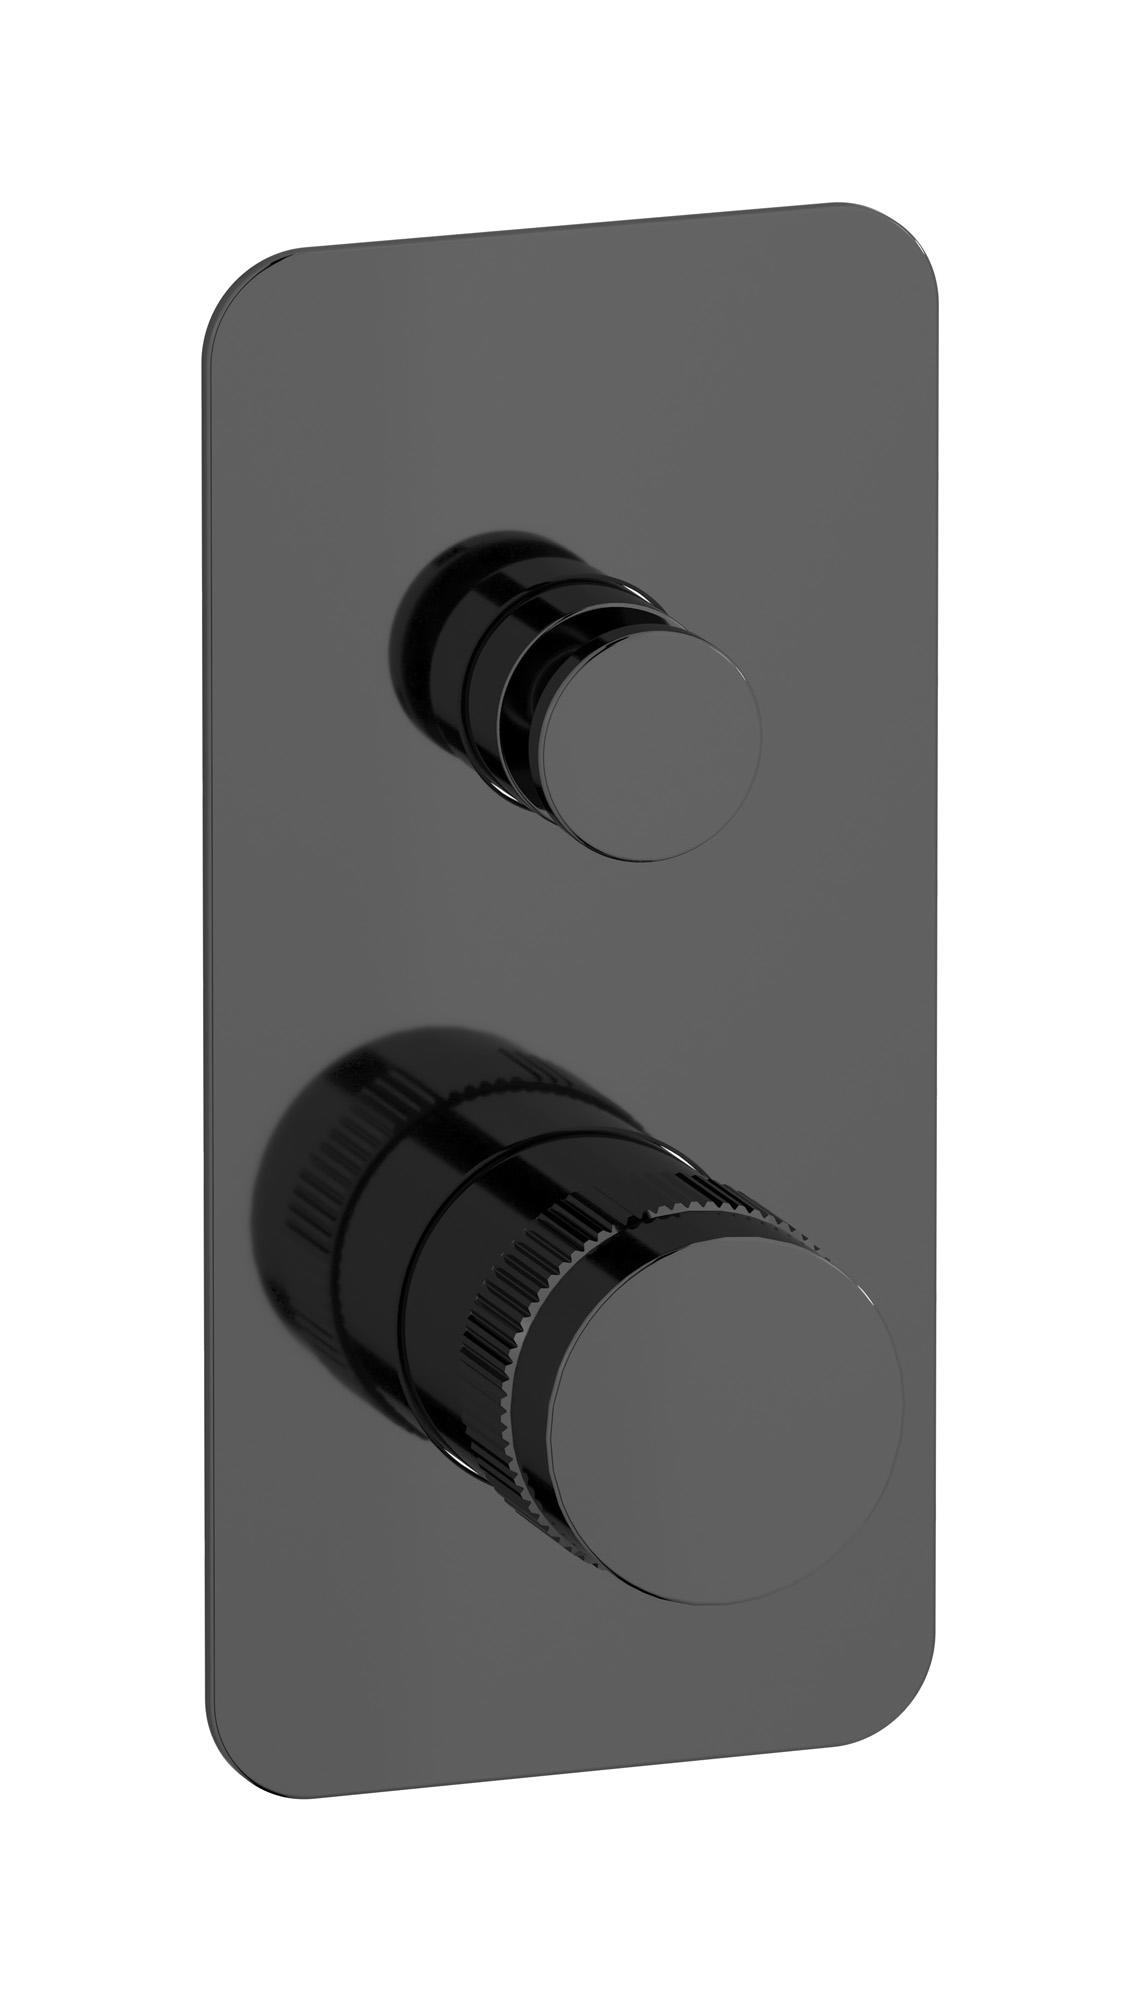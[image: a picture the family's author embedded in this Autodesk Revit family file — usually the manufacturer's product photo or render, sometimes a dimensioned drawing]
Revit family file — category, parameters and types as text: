
# Revit family: RX310
name_source: partatom
category: Apparecchi idraulici
units: mm (PartAtom-declared; Revit-internal decimal feet)

## family parameters
Basato su piano di lavoro = No
Condiviso = No
Mantieni orientamento annotazione = No
Numero OmniClass = 23.45.55.17
Punto di calcolo locali = No
Quota connettore circolare = Usa diametro
Sempre verticale = Sì
Taglio con vuoti quando caricato = No
Tipo di parte = Normale
Titolo OmniClass = Mixing Faucets

## types (12) — shared parameters
Cold water inlet = 10 mm  [stored 0.0328084 ft]
Commenti sul tipo = Exposed parts for manual wall hydroprogressive mixer with 2 ways diverter
Connessione CW = No
Connessione HW = No
Connessione di scarico = No
Connessione di ventilazione = No
Descrizione = Exposed parts for manual wall hydroprogressive mixer with 2 ways diverter
Hot water inlet = 10 mm  [stored 0.0328084 ft]
Produttore = IB Rubinetterie S.p.A.
URL = https://www.weareib.it
zero-valued in all types: Prospetto di default

## per-type parameters (varying)
| type | Finishes surface | Immagine tipo | Modello |
| Chrome | IB_Chrome | RX310CC.jpg | RX310CC |
| Black Chrome | IB_Black chrome | RX310CF.jpg | RX310CF |
| Brushed Black Chrome | IB_Brushed black chrome | RX310CS.jpg | RX310CS |
| Pale Gold | IB_Pale gold | RX310II.jpg | RX310II |
| Brushed Pale Gold | IB_brushed pale gold | RX310IS.jpg | RX310IS |
| Matt Black | IB_matt black | RX310NP.jpg | RX310NP |
| Natural Brass | IB_Brass | RX310ON.jpg | RX310ON |
| Gold | IB_gold | RX310OO.jpg | RX310OO |
| Brushed Gold | IB_brushed gold | RX310OS.jpg | RX310OS |
| Rose Gold | IB_Rose gold | RX310RS.jpg | RX310RS |
| Brushed Rose Gold | IB_Brushed rose gold | RX310SR.jpg | RX310SR |
| Brushed Nickel | IB_Brushed nickel | RX310SS.jpg | RX310SS |

note: [stored X ft] marks values corroborated as IEEE doubles in the binary element streams (Revit-internal decimal feet)
